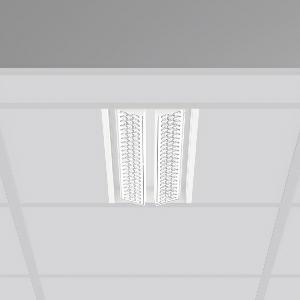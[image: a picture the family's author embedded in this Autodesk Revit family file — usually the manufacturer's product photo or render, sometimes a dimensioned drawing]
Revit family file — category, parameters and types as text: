
# Revit family: tx-move_901738_002_1_3c1b
name_source: partatom
category: Lighting Fixtures
units: mm (PartAtom-declared; Revit-internal decimal feet)

## family parameters
Cut with Voids When Loaded = No
Host = Face
Light Source = No
Part Type = Normal
Room Calculation Point = No
Round Connector Dimension = Use Diameter
Shared = No

## types (1)
- MultiLumen 1 (1 x LED Modul 840, 2675 lm, 4000)
    Apparent Load = 35 VA
    Approval mark = CE
    CIE Flux Codes = 65 90 98 100 100
    Color Rendering = 80
    Color Temperature = 4000
    Default Elevation = 1800 mm
    Description = Series: TX-MOVE
Einlege/Einbau-Flächenstrahler. Housing: sheet steel, powder-coated. 2xSwivel range: 90°. High-efficiency LED units with optimum light control thanks to clear plastic (PC) lens optics. Spezielle Mikrostrukturen reduzieren Gelbsaum. Asymmetrical light distribution. Suitable for laying in grid ceiling module 625. Connected converter included in separate gearbox.Suitable for through-wiring.MultiLumen: Luminous flux adjustable in 3 steps. Accessories: Mounting frame for installation in suspended ceilings. Environmentally friendly and resource-saving due to replaceable and recyclable components. 
Colour: traffic white, matt (RAL 9016)
Length: 622 mm
Width: 190 mm
Height: 39 mm
Cut-out length: 602 mm
Cut-out width: 174 mm
Recess height: 100 mm
Lamp: LED
Socket: without socket
Colour temperature: 4000K
Colour rendering index (CRI): 80
System power: 35 W
Rated luminous flux: 5350 lm
Luminous efficiency: 153 lm/W
System power 2: 47 W
Rated luminous flux 2: 6950 lm
Luminous efficiency 2: 148 lm/W
System power 3: 68 W
Rated luminous flux 3: 9600 lm
Luminous efficiency 3: 141 lm/W
Control gear: Regulated power supply
Protection class: I
Type of protection: IP 20
    Height = 0 mm  [stored 0 ft]
    Lamp = 1 x LED Modul 840
    Lamp Light Flux = 2675 lm
    Lamp count = 1
    Length = 622 mm
    Lifetime = 50000 h
    Luminous efficacy = 153 lm/W
    Manufacturer = RZB
    ModVariant = No
    Model = 901738.002.1
    Mounting Place = Ceiling, Wall
    Mounting Type = Recessed
    Number of Poles = 1
    OnlyDefault = Yes
    Power Factor = 1
    Product Name = TX-MOVE
    Product group = Recessed projectors
    ProductGroupID = 401
    Protection Class = Protection class I
    Protection Degree = IP 20
    RLX_Detail_Level = 1
    RLX_Emergency_Light_Flux = 0 lm
    RLX_Emergency_Type = 0
    RLX_Emergency_Type_DB = No
    RlxData = <blob elided: 54893 chars, md5=efd044ab>
    Socket = socket
    Standby Power = 0 W
    System Light Flux = 5350 lm
    System Power = 35 W
    Type Comments = MultiLumen 1
    Type Image = 901737.002.jpg
    URL = http://relux.com
    VarID = multilumen_1
    Voltage = 230 V
    Voltage Range = 220-240 V
    Weight = 0.00 kg
    Width = 190 mm  [stored 0.62336 ft]

note: [stored X ft] marks values corroborated as IEEE doubles in the binary element streams (Revit-internal decimal feet)

## geometry (parser evidence)
native form markers: Blend x4, Sweep x14
no freeform markers — native parametric forms only
